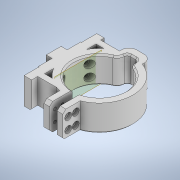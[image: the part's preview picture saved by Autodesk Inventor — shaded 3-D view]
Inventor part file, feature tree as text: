
AUTODESK INVENTOR PART (.ipt)
format: ipt  version: 2020 (Build 240168000, 168)  size: 469,504 bytes
history: native  units: mm
features: extrude x16, sketch x16, fillet x2, chamfer x2, other x1
ambient origin geometry x8: Origin, YZ Plane, XZ Plane, XY Plane, X Axis, Y Axis, Z Axis, Center Point
bodies: Solide1 (feature_tree)
feature tree (37):
  extrude  "Extrusion1"  Depth=88.4mm
  extrude  "Extrusion2"  Depth=35.0mm TaperAngle=0.0deg
  extrude  "Extrusion3"  Depth=68.5mm
  extrude  "Extrusion4"  TaperAngle=0.0deg  [1 undecoded]
  fillet  "Congé1"  Radius=20.0mm
  fillet  "Congé2"  Radius=30.0mm
  extrude  "Extrusion5"  Depth=15.0mm
  extrude  "Extrusion6"  Depth=9.95mm
  extrude  "Extrusion7"  Depth=35.0mm TaperAngle=0.0deg
  chamfer  "Chanfrein1"  Distance=15.0mm
  extrude  "Extrusion8"  Depth=15.0mm
  extrude  "Extrusion9"  Depth=7.5mm
  extrude  "Extrusion10"  Depth=10.0mm
  extrude  "Extrusion11"  Depth=35.0mm TaperAngle=0.0deg
  extrude  "Extrusion12"  Depth=10.0mm
  extrude  "Extrusion13"  Depth=4.0mm
  extrude  "Extrusion14"  Depth=30.0mm
  other  "Plan de construction2"
  extrude  "Extrusion15"  Depth=25.0mm
  extrude  "Extrusion16"  Depth=12.5mm
  chamfer  "Chanfrein3"  Distance=35.0mm
  sketch  "Esquisse1"
  sketch  "Esquisse2"
  sketch  "Esquisse3"
  sketch  "Esquisse4"
  sketch  "Esquisse5"
  sketch  "Esquisse6"
  sketch  "Esquisse7"
  sketch  "Esquisse10"
  sketch  "Esquisse11"
  sketch  "Esquisse12"
  sketch  "Esquisse13"
  sketch  "Esquisse14"
  sketch  "Esquisse15"
  sketch  "Esquisse16"
  sketch  "Esquisse19"
  sketch  "Esquisse20"
note: 1 required parameter value undecoded (feature->parameter linkage not recoverable at this tier; creation-order binding heuristic only, values carry confidence <= 0.55)
